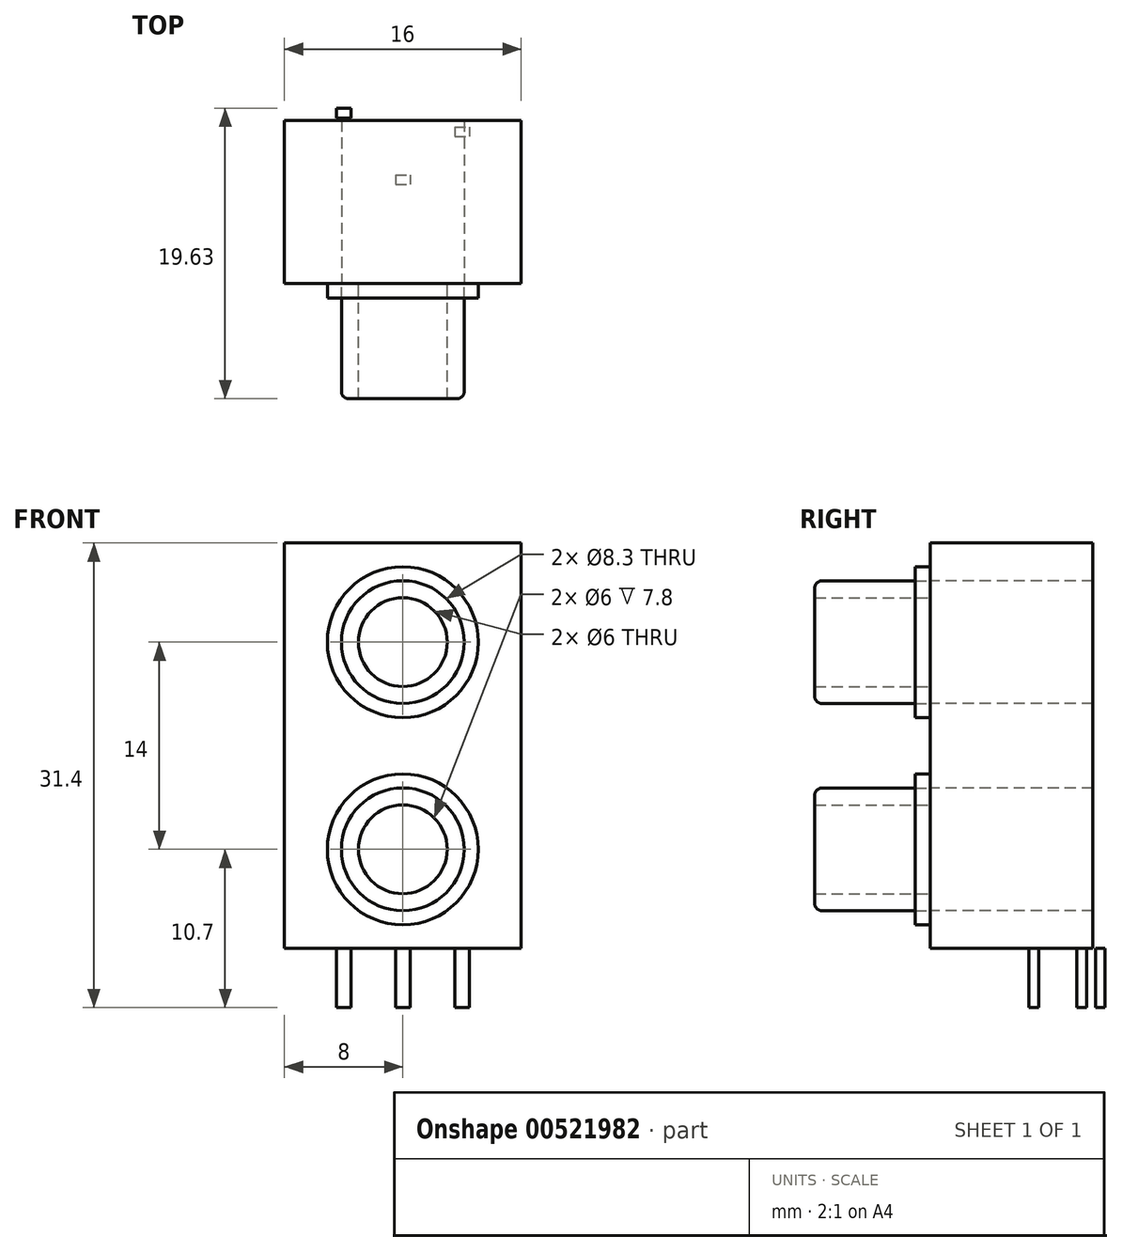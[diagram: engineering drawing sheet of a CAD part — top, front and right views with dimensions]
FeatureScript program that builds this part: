
annotation { "Feature Type Name" : "Feature", "Feature Type Description" : "" }
export const myFeature = defineFeature(function(context is Context, id is Id, definition is map)
    precondition{}
    {
        {
            var Q0;
            Q0=qCreatedBy(makeId("Front.planeOp"),FACE);
            var sketch = newSketch(context, id + "F0", { "sketchPlane" : qUnion([Q0])});
            skCircle(sketch, "E0", {"center": v(0, 20.7) * mm, "radius": 4.15 * mm});
            skCircle(sketch, "E1", {"center": v(0, 6.7) * mm, "radius": 4.15 * mm});
            skCircle(sketch, "E2", {"center": v(0, 20.7) * mm, "radius": 3 * mm});
            skCircle(sketch, "E3", {"center": v(0, 6.7) * mm, "radius": 3 * mm});
            skLineSegment(sketch, "E4", {"start": v(-21.93, 13.7) * mm, "end": v(28.04, 13.7) * mm, "construction": true});
            skLineSegment(sketch, "E5.bottom", {"start": v(-8, 27.4) * mm, "end": v(8, 27.4) * mm});
            skLineSegment(sketch, "E5.top", {"start": v(-8, 0) * mm, "end": v(8, 0) * mm});
            skLineSegment(sketch, "E5.left", {"start": v(-8, 27.4) * mm, "end": v(-8, 0) * mm});
            skLineSegment(sketch, "E5.right", {"start": v(8, 27.4) * mm, "end": v(8, 0) * mm});
            skSolve(sketch);
        }
        {
            var Q0;
            Q0=qCreatedBy(makeId("Front.planeOp"),FACE);
            var sketch = newSketch(context, id + "F1", { "sketchPlane" : qUnion([Q0])});
            skCircle(sketch, "E6", {"center": v(0, 20.7) * mm, "radius": 5.1 * mm});
            skCircle(sketch, "E7", {"center": v(0, 6.7) * mm, "radius": 5.1 * mm});
            skCircle(sketch, "E8", {"center": v(0, 20.7) * mm, "radius": 3 * mm});
            skCircle(sketch, "E9", {"center": v(0, 6.7) * mm, "radius": 3 * mm});
            skSolve(sketch);
        }
        {
            var Q0;
            Q0=makeQuery(id+"F0.imprint","IMPRINT",FACE,{"disambiguationData":[TD([[makeQuery(id+"F0.imprint","IMPRINT",EDGE,{"derivedFrom":sQuery(id+"F0.wireOp",EDGE,"E0")}),1.0]])]});
            var Q1;
            Q1=makeQuery(id+"F0.imprint","IMPRINT",FACE,{"disambiguationData":[TD([[makeQuery(id+"F0.imprint","IMPRINT",EDGE,{"derivedFrom":sQuery(id+"F0.wireOp",EDGE,"E1")}),1.0]])]});
            extrude(context, id + "F2", {"entities" : qUnion([Q0, Q1]), "depth" : 7.8 * mm, "offsetDistance" : 25 * mm});
        }
        {
            var Q0;
            Q0=makeQuery(id+"F2.opExtrude","CAP_EDGE",EDGE,{"disambiguationData":[OSD([sQuery(id+"F0.wireOp",EDGE,"E0")])],"isStart":false});
            var Q1;
            Q1=makeQuery(id+"F2.opExtrude","CAP_EDGE",EDGE,{"disambiguationData":[OSD([sQuery(id+"F0.wireOp",EDGE,"E1")])],"isStart":false});
            fillet(context, id + "F3", {"entities" : qUnion([Q0, Q1]), "radius" : 0.5 * mm, "tangentPropagation" : true, "allowEdgeOverflow" : false});
        }
        {
            var Q0;
            Q0 = qSketchRegion(id + "F1", true);
            extrude(context, id + "F4", {"entities" : qUnion([Q0]), "depth" : 1 * mm, "offsetDistance" : 25 * mm});
        }
        {
            var Q0;
            Q0=makeQuery(id+"F0.imprint","IMPRINT",FACE,{"disambiguationData":[TD([[makeQuery(id+"F0.imprint","IMPRINT",EDGE,{"derivedFrom":sQuery(id+"F0.wireOp",EDGE,"E0")}),-1.0]])]});
            extrude(context, id + "F5", {"entities" : qUnion([Q0]), "oppositeDirection" : true, "depth" : 11 * mm, "offsetDistance" : 25 * mm});
        }
        {
            var Q0;
            Q0=qCreatedBy(makeId("Top.planeOp"),FACE);
            var sketch = newSketch(context, id + "F6", { "sketchPlane" : qUnion([Q0])});
            skLineSegment(sketch, "E10.bottom", {"start": v(-0.5, 7.32) * mm, "end": v(0.5, 7.32) * mm});
            skLineSegment(sketch, "E10.top", {"start": v(-0.5, 6.68) * mm, "end": v(0.5, 6.68) * mm});
            skLineSegment(sketch, "E10.left", {"start": v(-0.5, 7.32) * mm, "end": v(-0.5, 6.67) * mm});
            skLineSegment(sketch, "E10.right", {"start": v(0.5, 7.32) * mm, "end": v(0.5, 6.67) * mm});
            skLineSegment(sketch, "E11", {"start": v(0, 7.32) * mm, "end": v(0, 6.68) * mm, "construction": true});
            skLineSegment(sketch, "E12", {"start": v(-0.5, 7) * mm, "end": v(0.5, 7) * mm, "construction": true});
            skLineSegment(sketch, "E13.bottom", {"start": v(-4.5, 11.82) * mm, "end": v(-3.5, 11.82) * mm});
            skLineSegment(sketch, "E13.top", {"start": v(-4.5, 11.18) * mm, "end": v(-3.5, 11.18) * mm});
            skLineSegment(sketch, "E13.left", {"start": v(-4.5, 11.82) * mm, "end": v(-4.5, 11.18) * mm});
            skLineSegment(sketch, "E13.right", {"start": v(-3.5, 11.82) * mm, "end": v(-3.5, 11.18) * mm});
            skLineSegment(sketch, "E14.bottom", {"start": v(3.5, 10.57) * mm, "end": v(4.5, 10.57) * mm});
            skLineSegment(sketch, "E14.top", {"start": v(3.5, 9.93) * mm, "end": v(4.5, 9.93) * mm});
            skLineSegment(sketch, "E14.left", {"start": v(3.5, 10.57) * mm, "end": v(3.5, 9.93) * mm});
            skLineSegment(sketch, "E14.right", {"start": v(4.5, 10.57) * mm, "end": v(4.5, 9.93) * mm});
            skLineSegment(sketch, "E15", {"start": v(4, 10.57) * mm, "end": v(4, 9.93) * mm, "construction": true});
            skLineSegment(sketch, "E16", {"start": v(3.5, 10.25) * mm, "end": v(4.5, 10.25) * mm, "construction": true});
            skLineSegment(sketch, "E17", {"start": v(-4, 11.18) * mm, "end": v(-4, 11.82) * mm, "construction": true});
            skLineSegment(sketch, "E18", {"start": v(-4.5, 11.5) * mm, "end": v(-3.5, 11.5) * mm, "construction": true});
            skSolve(sketch);
        }
        {
            var Q0;
            Q0 = qSketchRegion(id + "F6", true);
            extrude(context, id + "F7", {"entities" : qUnion([Q0]), "operationType" : NewBodyOperationType.ADD, "oppositeDirection" : true, "depth" : 4 * mm, "offsetDistance" : 25 * mm});
        }
    });
